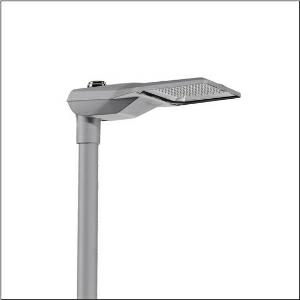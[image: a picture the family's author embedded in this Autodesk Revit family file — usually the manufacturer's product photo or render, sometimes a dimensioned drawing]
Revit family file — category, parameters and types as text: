
# Revit family: streetlight_sl_21_midi___stw1_0a_5xe7e47n08nb_2a9b
name_source: partatom
category: Lighting Fixtures
units: mm (PartAtom-declared; Revit-internal decimal feet)

## family parameters
Cut with Voids When Loaded = No
Host = Face
Light Source = No
Part Type = Normal
Room Calculation Point = No
Round Connector Dimension = Use Diameter
Shared = No

## types (1)
- --- (1 x LED, 23710 lm, 151.2 W, 4000K)
    Apparent Load = 151 VA
    CIE Flux Codes = 39 75 98 100 100
    Color Rendering = 70
    Color Temperature = 4000K
    Default Elevation = 1800 mm
    Description = Streetlight SL 21 midi, mast luminaire, primary light control with lens, of PMMA, primary optical cover: cover, of toughened safety glass, transparent, light distribution: STW1.0a, light emission: direct distribution, primary light characteristic: asymmetric, installation type: side-entry, LED, 3G 2.5mm², High Power LED, rated luminous flux: 23.710lm, luminous efficacy: 157lm/W, light colour: 740, colour temperature: 4000K, control gear: NEMA (7pin), control: overheat protection, pre-setting: linear dimming characteristic, constant luminous flux control, time-dependent luminous flux control, flexible luminous flux parameterisation, mains connection: 220..240V, AC, 50/60Hz, connection cable pre-assembled, cable length: 12,5m, wiring characteristics: H05VV-F, start of lifetime: 151W, end of service life: 157W, reduction: 70W, luminaire housing, of diecast aluminium (EN AC-44300), powder-coated, Siteco® metallic grey (DB 702S), corrosivity category C5 mid according to DIN EN ISO 12944, multi-level sealing system, sealing non-destructively replaceable, inclination adjustable: 0°, 5°, 10°, 15°, length: 644mm, width: 335mm, height: 110mm, spigot size: 42mm (side-entry), mounting height: 4..8m, protection rating (complete): IP66, insulation class (complete): insulation class I (protective earthing), certification: CE, ENEC, ENEC+, VDE, impact resistance: IK10, permissible operating ambient temperature for outdoor applications: -40..+50°C, standard-compliant lighting for roads and squares, packaging unit: 1 piece

Light Distribution: STW1.0a
    Height = 111 mm
    Lamp = 1 x LED
    Lamp Light Flux = 23710 lm
    Lamp Power = 151.2 W
    Lamp count = 1
    Length = 644 mm
    Luminous efficacy = 157 lm/W
    Manufacturer = Siteco
    ModVariant = No
    Model = 5XE7E47N08NB
    Number of Poles = 1
    OnlyDefault = Yes
    Power Factor = 1
    Product Name = Streetlight SL 21 midi | STW1.0a
    Product group = mast luminaire | pylon top
    ProductGroupID = 6100
    Protection Class = Protection class I
    Protection Degree = IP 66
    RLX_Detail_Level = 1
    RLX_Emergency_Light_Flux = 0 lm
    RLX_Emergency_Type = 0
    RLX_Emergency_Type_DB = No
    RlxData = <blob elided: 26685 chars, md5=e41e8b98>
    Socket = socket
    Standby Power = 0 W
    System Light Flux = 23710 lm
    System Power = 151 W
    Type Comments = factory setting: luminous flux: 100 % | dim-lin: 254 | 802 mA
    Type Image = l_1294377.jpg
    URL = http://relux.com
    VarID = @adj_156375
    Voltage = 0 V
    Weight = 0.00 kg
    Width = 336 mm

## geometry (parser evidence)
native form markers: Blend x4, Sweep x9
no freeform markers — native parametric forms only
